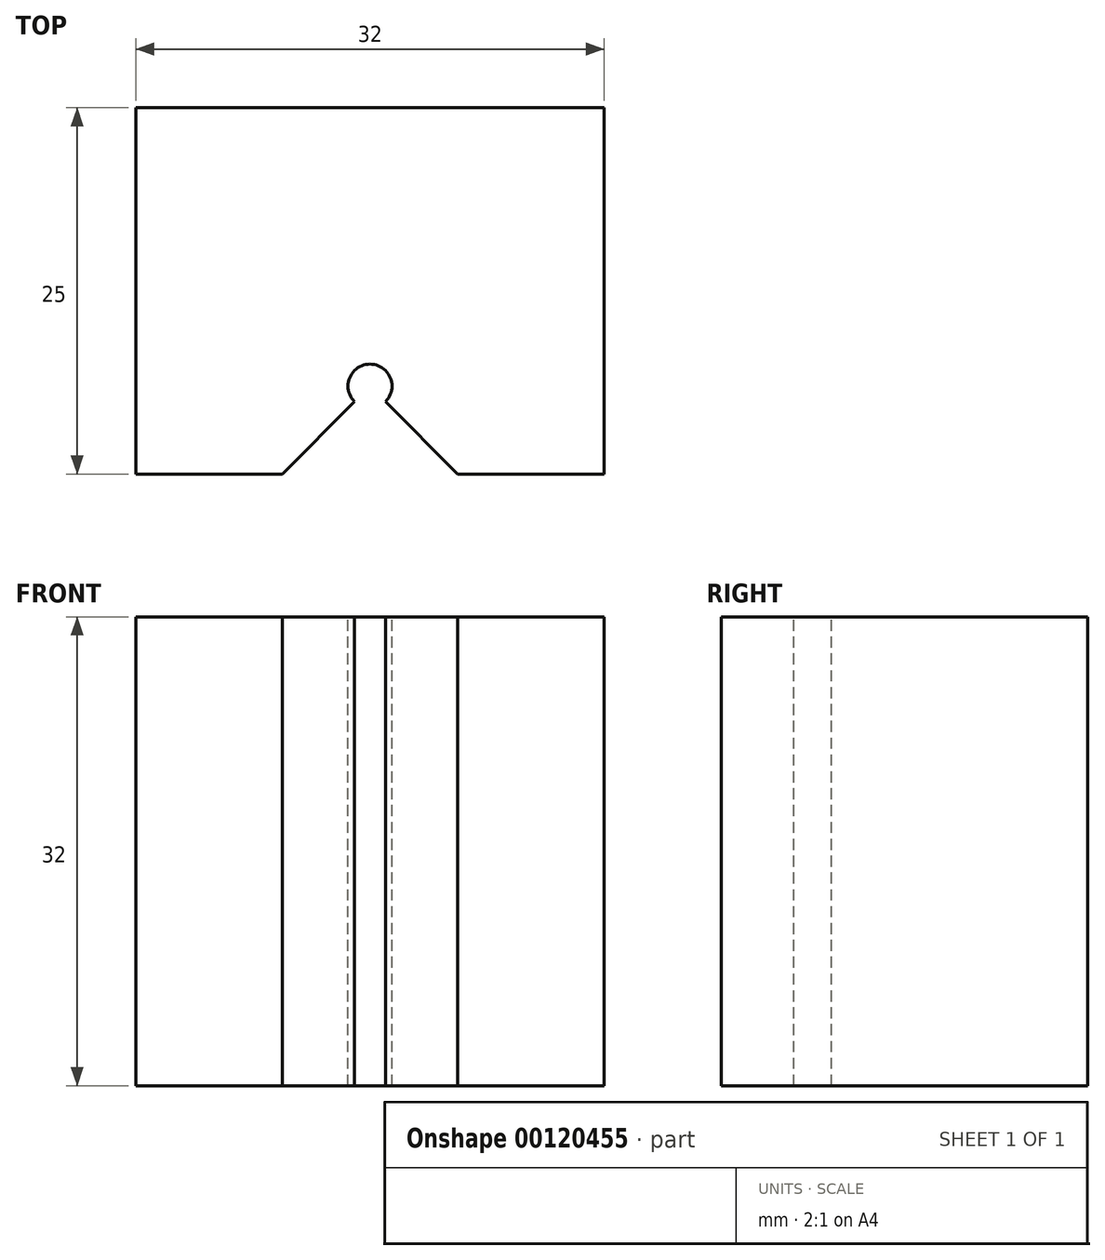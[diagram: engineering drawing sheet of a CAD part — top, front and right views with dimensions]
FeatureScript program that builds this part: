
annotation { "Feature Type Name" : "Feature", "Feature Type Description" : "" }
export const myFeature = defineFeature(function(context is Context, id is Id, definition is map)
    precondition{}
    {
        {
            var Q0;
            Q0=qCreatedBy(makeId("Front.planeOp"),FACE);
            var sketch = newSketch(context, id + "F0", { "sketchPlane" : qUnion([Q0])});
            skLineSegment(sketch, "E0.bottom", {"start": v(16, 16) * mm, "end": v(-16, 16) * mm});
            skLineSegment(sketch, "E0.top", {"start": v(16, -16) * mm, "end": v(-16, -16) * mm});
            skLineSegment(sketch, "E0.left", {"start": v(16, 16) * mm, "end": v(16, -16) * mm});
            skLineSegment(sketch, "E0.right", {"start": v(-16, 16) * mm, "end": v(-16, -16) * mm});
            skPoint(sketch, "E0.middle", {"position": v(0, 0) * mm});
            skSolve(sketch);
        }
        {
            var Q0;
            Q0 = qSketchRegion(id + "F0", true);
            extrude(context, id + "F1", {"entities" : qUnion([Q0]), "oppositeDirection" : true, "depth" : 25 * mm});
        }
        {
            var Q0;
            Q0=makeQuery(id+"F1.opExtrude","SWEPT_FACE",FACE,{"disambiguationData":[OSD([sQuery(id+"F0.wireOp",EDGE,"E0.bottom")])]});
            var sketch = newSketch(context, id + "F2", { "sketchPlane" : qUnion([Q0])});
            skLineSegment(sketch, "E1", {"start": v(0, 25) * mm, "end": v(0, 0) * mm, "construction": true});
            skLineSegment(sketch, "E2", {"start": v(-6, 0) * mm, "end": v(0, 6) * mm});
            skLineSegment(sketch, "E3", {"start": v(0, 6) * mm, "end": v(6, 0) * mm});
            skLineSegment(sketch, "E4", {"start": v(6, 0) * mm, "end": v(-6, 0) * mm});
            skCircle(sketch, "E5", {"center": v(0, 6) * mm, "radius": 1.5 * mm});
            skSolve(sketch);
        }
        {
            var Q0;
            Q0 = qSketchRegion(id + "F2", true);
            extrude(context, id + "F3", {"entities" : qUnion([Q0]), "operationType" : NewBodyOperationType.REMOVE, "endBound" : BoundingType.THROUGH_ALL, "oppositeDirection" : true, "depth" : 25 * mm});
        }
    });
